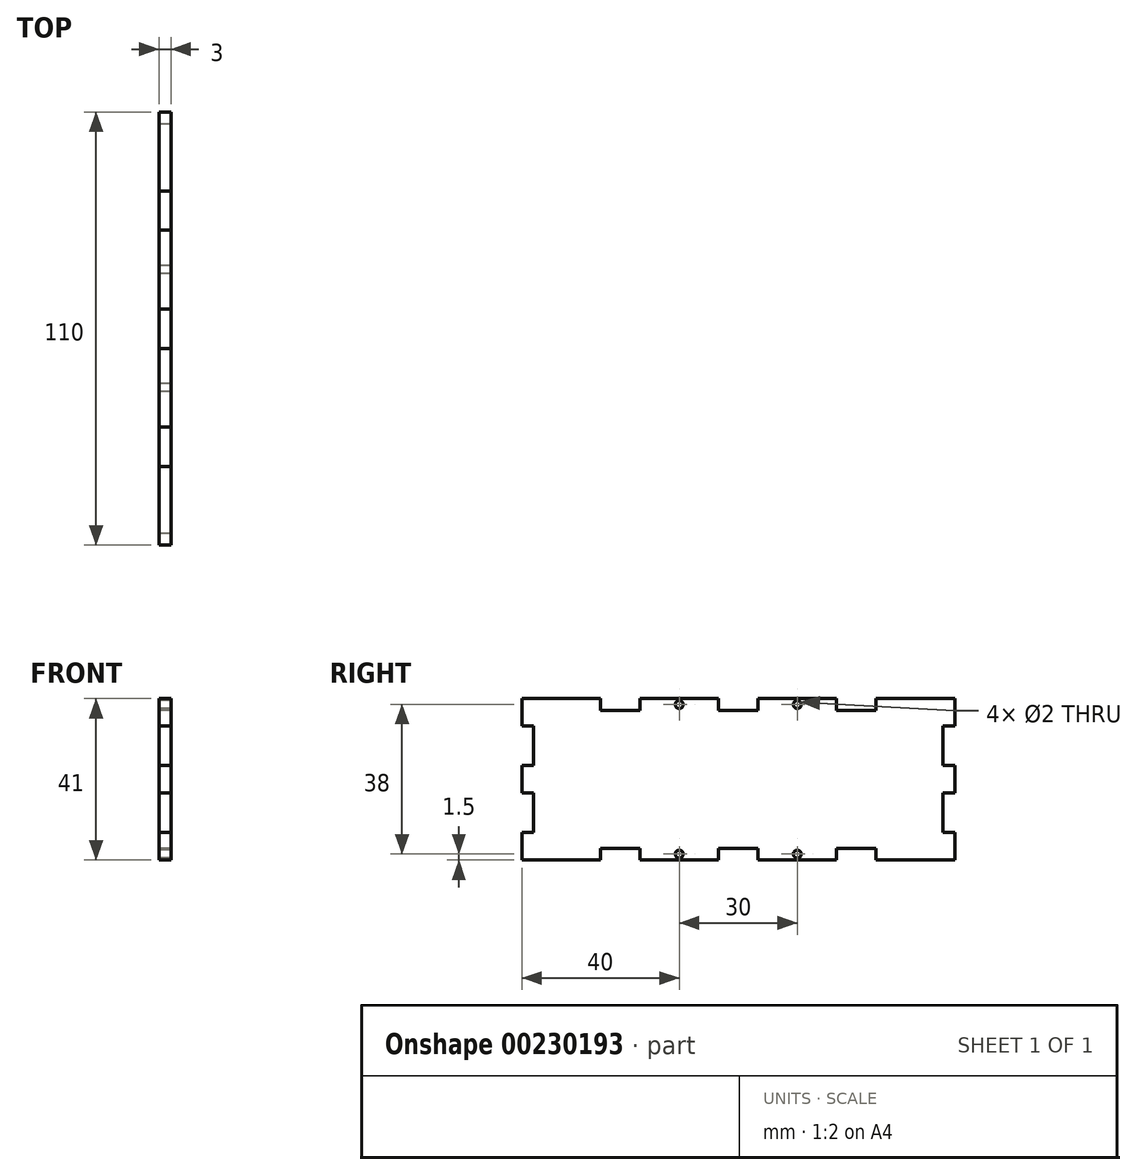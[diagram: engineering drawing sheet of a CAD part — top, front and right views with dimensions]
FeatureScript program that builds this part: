
annotation { "Feature Type Name" : "Feature", "Feature Type Description" : "" }
export const myFeature = defineFeature(function(context is Context, id is Id, definition is map)
    precondition{}
    {
        {
            var Q0;
            Q0=qCreatedBy(makeId("Right.planeOp"),FACE);
            var sketch = newSketch(context, id + "F0", { "sketchPlane" : qUnion([Q0])});
            skLineSegment(sketch, "E0", {"start": v(0, 0) * mm, "end": v(0, 7) * mm});
            skLineSegment(sketch, "E1", {"start": v(0, 7) * mm, "end": v(-3, 7) * mm});
            skLineSegment(sketch, "E2", {"start": v(-3, 7) * mm, "end": v(-3, 17) * mm});
            skLineSegment(sketch, "E3", {"start": v(-3, 17) * mm, "end": v(0, 17) * mm});
            skLineSegment(sketch, "E4", {"start": v(0, 17) * mm, "end": v(0, 24) * mm});
            skLineSegment(sketch, "E5", {"start": v(0, 24) * mm, "end": v(-3, 24) * mm});
            skLineSegment(sketch, "E6", {"start": v(-3, 24) * mm, "end": v(-3, 34) * mm});
            skLineSegment(sketch, "E7", {"start": v(-3, 34) * mm, "end": v(0, 34) * mm});
            skLineSegment(sketch, "E8", {"start": v(0, 34) * mm, "end": v(0, 41) * mm});
            skLineSegment(sketch, "E9", {"start": v(0, 41) * mm, "end": v(-20, 41) * mm});
            skLineSegment(sketch, "E10", {"start": v(-20, 41) * mm, "end": v(-20, 38) * mm});
            skLineSegment(sketch, "E11", {"start": v(-20, 38) * mm, "end": v(-30, 38) * mm});
            skLineSegment(sketch, "E12", {"start": v(-30, 38) * mm, "end": v(-30, 41) * mm});
            skLineSegment(sketch, "E13", {"start": v(-30, 41) * mm, "end": v(-50, 41) * mm});
            skLineSegment(sketch, "E14", {"start": v(-50, 41) * mm, "end": v(-50, 38) * mm});
            skLineSegment(sketch, "E15", {"start": v(-50, 38) * mm, "end": v(-55, 38) * mm});
            skLineSegment(sketch, "E16", {"start": v(-55, 3) * mm, "end": v(-50, 3) * mm});
            skLineSegment(sketch, "E17", {"start": v(-50, 3) * mm, "end": v(-50, 0) * mm});
            skLineSegment(sketch, "E18", {"start": v(-50, 0) * mm, "end": v(-30, 0) * mm});
            skLineSegment(sketch, "E19", {"start": v(-30, 0) * mm, "end": v(-30, 3) * mm});
            skLineSegment(sketch, "E20", {"start": v(-30, 3) * mm, "end": v(-20, 3) * mm});
            skLineSegment(sketch, "E21", {"start": v(-20, 3) * mm, "end": v(-20, 0) * mm});
            skLineSegment(sketch, "E22", {"start": v(-20, 0) * mm, "end": v(0, 0) * mm});
            skPoint(sketch, "E23.endSnap0", {"position": v(-40, 41) * mm});
            skCircle(sketch, "E24", {"center": v(-40, 39.5) * mm, "radius": 1 * mm});
            skCircle(sketch, "E25.MirrorC", {"center": v(-40, 1.5) * mm, "radius": 1 * mm});
            skCircle(sketch, "E26.MirrorC", {"center": v(-70, 39.5) * mm, "radius": 1 * mm});
            skLineSegment(sketch, "E27.MirrorCS", {"start": v(-55, 3) * mm, "end": v(-60, 3) * mm});
            skLineSegment(sketch, "E28.MirrorCS", {"start": v(-80, 0) * mm, "end": v(-80, 3) * mm});
            skLineSegment(sketch, "E29.MirrorCS", {"start": v(-80, 38) * mm, "end": v(-80, 41) * mm});
            skLineSegment(sketch, "E30.MirrorCS", {"start": v(-90, 38) * mm, "end": v(-80, 38) * mm});
            skLineSegment(sketch, "E31.MirrorCS", {"start": v(-110, 7) * mm, "end": v(-107, 7) * mm});
            skLineSegment(sketch, "E32.MirrorCS", {"start": v(-107, 7) * mm, "end": v(-107, 17) * mm});
            skLineSegment(sketch, "E33.MirrorCS", {"start": v(-110, 0) * mm, "end": v(-110, 7) * mm});
            skLineSegment(sketch, "E34.MirrorCS", {"start": v(-80, 3) * mm, "end": v(-90, 3) * mm});
            skPoint(sketch, "E35.MirrorP", {"position": v(-70, 41) * mm});
            skLineSegment(sketch, "E36.MirrorCS", {"start": v(-60, 38) * mm, "end": v(-55, 38) * mm});
            skLineSegment(sketch, "E37.MirrorCS", {"start": v(-90, 0) * mm, "end": v(-110, 0) * mm});
            skLineSegment(sketch, "E38.MirrorCS", {"start": v(-90, 3) * mm, "end": v(-90, 0) * mm});
            skLineSegment(sketch, "E39.MirrorCS", {"start": v(-60, 0) * mm, "end": v(-80, 0) * mm});
            skCircle(sketch, "E40.MirrorC", {"center": v(-70, 1.5) * mm, "radius": 1 * mm});
            skLineSegment(sketch, "E41.MirrorCS", {"start": v(-110, 41) * mm, "end": v(-90, 41) * mm});
            skLineSegment(sketch, "E42.MirrorCS", {"start": v(-110, 24) * mm, "end": v(-107, 24) * mm});
            skLineSegment(sketch, "E43.MirrorCS", {"start": v(-90, 41) * mm, "end": v(-90, 38) * mm});
            skLineSegment(sketch, "E44.MirrorCS", {"start": v(-110, 34) * mm, "end": v(-110, 41) * mm});
            skLineSegment(sketch, "E45.MirrorCS", {"start": v(-107, 17) * mm, "end": v(-110, 17) * mm});
            skLineSegment(sketch, "E46.MirrorCS", {"start": v(-80, 41) * mm, "end": v(-60, 41) * mm});
            skLineSegment(sketch, "E47.MirrorCS", {"start": v(-60, 3) * mm, "end": v(-60, 0) * mm});
            skLineSegment(sketch, "E48.MirrorCS", {"start": v(-60, 41) * mm, "end": v(-60, 38) * mm});
            skLineSegment(sketch, "E49.MirrorCS", {"start": v(-107, 34) * mm, "end": v(-110, 34) * mm});
            skLineSegment(sketch, "E50.MirrorCS", {"start": v(-107, 24) * mm, "end": v(-107, 34) * mm});
            skLineSegment(sketch, "E51.MirrorCS", {"start": v(-110, 17) * mm, "end": v(-110, 24) * mm});
            skSolve(sketch);
        }
        {
            var Q0;
            Q0=makeQuery(id+"F0.imprint","IMPRINT",FACE,{"disambiguationData":[TD([[makeQuery(id+"F0.imprint","IMPRINT",EDGE,{"derivedFrom":sQuery(id+"F0.wireOp",EDGE,"E0")}),1.0]])]});
            extrude(context, id + "F1", {"entities" : qUnion([Q0]), "depth" : 3 * mm});
        }
    });
